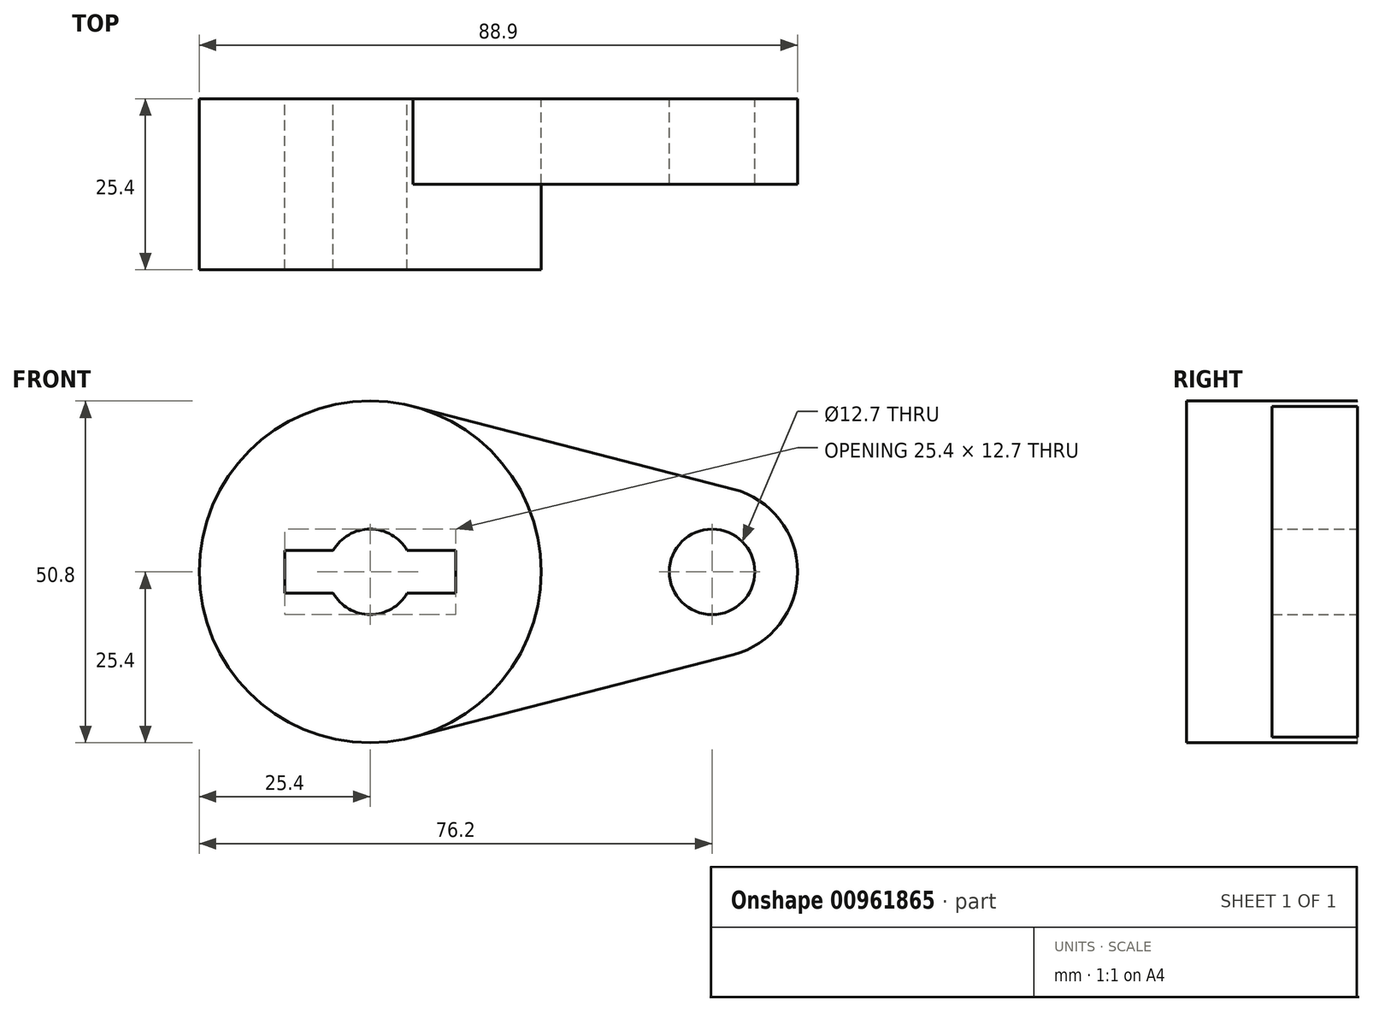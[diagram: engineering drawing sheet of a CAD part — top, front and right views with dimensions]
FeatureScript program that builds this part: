
annotation { "Feature Type Name" : "Feature", "Feature Type Description" : "" }
export const myFeature = defineFeature(function(context is Context, id is Id, definition is map)
    precondition{}
    {
        {
            var Q0;
            Q0=qCreatedBy(makeId("Front.planeOp"),FACE);
            var sketch = newSketch(context, id + "F0", { "sketchPlane" : qUnion([Q0])});
            skCircle(sketch, "E0", {"center": v(0, 0) * mm, "radius": 25.4 * mm});
            skCircle(sketch, "E1", {"center": v(50.8, 0) * mm, "radius": 12.7 * mm});
            skLineSegment(sketch, "E2", {"start": v(6.35, 24.6) * mm, "end": v(53.98, 12.3) * mm});
            skLineSegment(sketch, "E3", {"start": v(6.35, -24.6) * mm, "end": v(53.98, -12.3) * mm});
            skCircle(sketch, "E4", {"center": v(0, 0) * mm, "radius": 6.35 * mm});
            skCircle(sketch, "E5", {"center": v(50.8, 0) * mm, "radius": 6.35 * mm});
            skLineSegment(sketch, "E6.bottom", {"start": v(12.7, 3.18) * mm, "end": v(-12.7, 3.18) * mm});
            skLineSegment(sketch, "E6.top", {"start": v(12.7, -3.18) * mm, "end": v(-12.7, -3.18) * mm});
            skLineSegment(sketch, "E6.left", {"start": v(12.7, 3.18) * mm, "end": v(12.7, -3.18) * mm});
            skLineSegment(sketch, "E6.right", {"start": v(-12.7, 3.18) * mm, "end": v(-12.7, -3.18) * mm});
            skSolve(sketch);
        }
        {
            var Q0;
            {var subQ7=sQuery(id+"F0.wireOp",EDGE,"E6.left");Q0=makeQuery(id+"F0.imprint","IMPRINT",FACE,{"disambiguationData":[TD([[makeQuery(id+"F0.imprint","IMPRINT",EDGE,{"derivedFrom":subQ7}),1.0]])]});}
            extrude(context, id + "F1", {"entities" : qUnion([Q0]), "depth" : 25.4 * mm, "offsetDistance" : 25.4 * mm});
        }
        {
            var Q0;
            {var subQ0=sQuery(id+"F0.wireOp",EDGE,"E2");Q0=makeQuery(id+"F0.imprint","IMPRINT",FACE,{"disambiguationData":[TD([[makeQuery(id+"F0.imprint","IMPRINT",EDGE,{"derivedFrom":subQ0}),-1.0]])]});}
            var Q1;
            Q1=makeQuery(id+"F0.imprint","IMPRINT",FACE,{"disambiguationData":[TD([[makeQuery(id+"F0.imprint","IMPRINT",EDGE,{"derivedFrom":sQuery(id+"F0.wireOp",EDGE,"E5")}),-1.0]])]});
            extrude(context, id + "F2", {"entities" : qUnion([Q0, Q1]), "depth" : 12.7 * mm, "offsetDistance" : 25.4 * mm});
        }
    });
